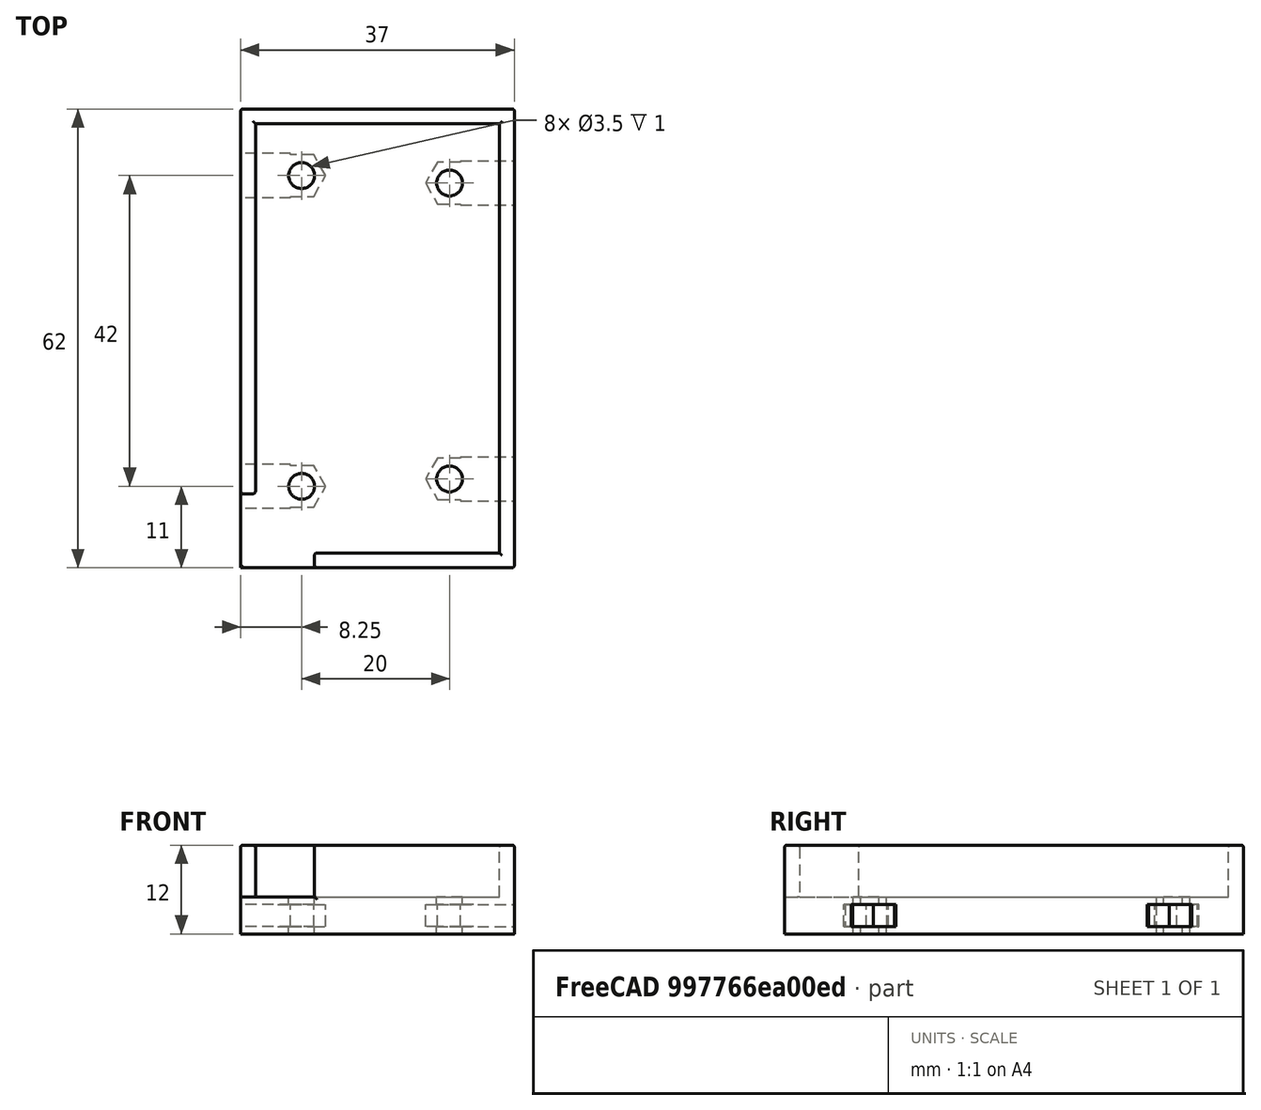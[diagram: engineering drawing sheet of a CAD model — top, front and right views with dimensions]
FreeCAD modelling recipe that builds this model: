
FCSTD DOCUMENT  (FreeCAD 0.19R14555 (Git shallow))
Label: Soporte Bateria
License: All rights reserved
LicenseURL: http://en.wikipedia.org/wiki/All_rights_reserved
objects: Part::Box×7, Part::MultiFuse×5, Part::Cylinder×4, Part::Prism×4, Part::Cut×3, Part::Fillet×2
note: 25 computed .brp shape members not serialized (recipe doc carries the construction recipe); baked Part::Feature solids carry a one-line shape summary decoded from their .brp

FEATURE [Part::Box] Box  label="Cubo"
  AttacherType = Attacher::AttachEngine3D
  Height = 10
  Length = 33
  Placement = pos=(0,0,5) rot=(0,0,1;0rad)
  Width = 58
FEATURE [Part::Box] Box001  label="Cubo001"
  AttacherType = Attacher::AttachEngine3D
  Height = 12
  Length = 37
  Placement = pos=(-2,-2,0) rot=(0,0,1;0rad)
  Width = 62
FEATURE [Part::Cut] Cut
  Base = -> Box001
  Tool = -> Box
FEATURE [Part::Box] Box002  label="Cubo002"
  AttacherType = Attacher::AttachEngine3D
  Height = 10
  Length = 10
  Placement = pos=(-2,-2,5) rot=(0,0,1;0rad)
  Width = 10
FEATURE [Part::Cut] Cut001
  Base = -> Cut
  Tool = -> Box002
FEATURE [Part::Cylinder] Cylinder004  label="Cilindro004"
  Angle = 360
  AttacherType = Attacher::AttachEngine3D
  Height = 20
  Placement = pos=(34,7.5,-1) rot=(0,0,1;0rad)
  Radius = 1.75
FEATURE [Part::Prism] Prism002  label="Prisma002"
  AttacherType = Attacher::AttachEngine3D
  Circumradius = 3.25
  FirstAngle = 0
  Height = 3
  Placement = pos=(34,7.5,3) rot=(0,0,1;1.5708rad)
  Polygon = 6
  SecondAngle = 0
FEATURE [Part::Box] Box003  label="Cubo003"
  AttacherType = Attacher::AttachEngine3D
  Height = 3
  Length = 6
  Placement = pos=(31,9,3) rot=(0,0,1;0rad)
  Width = 20
FEATURE [Part::MultiFuse] Fusion
  Placement = pos=(13.75,17,-2) rot=(0,0,1;1.5708rad)
  Shapes = -> [Box003,Prism002,Cylinder004]
FEATURE [Part::Box] Box004  label="Cubo004"
  AttacherType = Attacher::AttachEngine3D
  Height = 3
  Length = 6
  Placement = pos=(31,9,3) rot=(0,0,1;0rad)
  Width = 20
FEATURE [Part::Cylinder] Cylinder005  label="Cilindro005"
  Angle = 360
  AttacherType = Attacher::AttachEngine3D
  Height = 20
  Placement = pos=(34,7.5,-1) rot=(0,0,1;0rad)
  Radius = 1.75
FEATURE [Part::Prism] Prism003  label="Prisma003"
  AttacherType = Attacher::AttachEngine3D
  Circumradius = 3.25
  FirstAngle = 0
  Height = 3
  Placement = pos=(34,7.5,3) rot=(0,0,1;1.5708rad)
  Polygon = 6
  SecondAngle = 0
FEATURE [Part::MultiFuse] Fusion001
  Placement = pos=(13.75,-25,-2) rot=(0,0,1;1.5708rad)
  Shapes = -> [Box004,Prism003,Cylinder005]
FEATURE [Part::Prism] Prism004  label="Prisma004"
  AttacherType = Attacher::AttachEngine3D
  Circumradius = 3.25
  FirstAngle = 0
  Height = 3
  Placement = pos=(34,7.5,3) rot=(0,0,1;1.5708rad)
  Polygon = 6
  SecondAngle = 0
FEATURE [Part::Cylinder] Cylinder006  label="Cilindro006"
  Angle = 360
  AttacherType = Attacher::AttachEngine3D
  Height = 20
  Placement = pos=(34,7.5,-1) rot=(0,0,1;0rad)
  Radius = 1.75
FEATURE [Part::Box] Box005  label="Cubo005"
  AttacherType = Attacher::AttachEngine3D
  Height = 3
  Length = 6
  Placement = pos=(31,9,3) rot=(0,0,1;0rad)
  Width = 20
FEATURE [Part::MultiFuse] Fusion002
  Placement = pos=(18.75,44,-2) rot=(0,0,1;-1.5708rad)
  Shapes = -> [Box005,Prism004,Cylinder006]
FEATURE [Part::Cylinder] Cylinder007  label="Cilindro007"
  Angle = 360
  AttacherType = Attacher::AttachEngine3D
  Height = 20
  Placement = pos=(34,7.5,-1) rot=(0,0,1;0rad)
  Radius = 1.75
FEATURE [Part::Prism] Prism005  label="Prisma005"
  AttacherType = Attacher::AttachEngine3D
  Circumradius = 3.25
  FirstAngle = 0
  Height = 3
  Placement = pos=(34,7.5,3) rot=(0,0,1;1.5708rad)
  Polygon = 6
  SecondAngle = 0
FEATURE [Part::Box] Box006  label="Cubo006"
  AttacherType = Attacher::AttachEngine3D
  Height = 3
  Length = 6
  Placement = pos=(31,9,3) rot=(0,0,1;0rad)
  Width = 20
FEATURE [Part::MultiFuse] Fusion003
  Placement = pos=(18.75,84,-2) rot=(0,0,-1;1.5708rad)
  Shapes = -> [Box006,Prism005,Cylinder007]
FEATURE [Part::MultiFuse] Fusion004
  Shapes = -> [Fusion,Fusion001,Fusion002,Fusion003]
FEATURE [Part::Cut] Cut002
  Base = -> Cut001
  Tool = -> Fusion004
FEATURE [Part::Fillet] Fillet
  Base = -> Cut002
  Edges = 11 edges r=0.3: [Edge4,Edge6,Edge15,Edge16,Edge30,Edge31,Edge34,Edge36,Edge37,Edge38,Edge39]
FEATURE [Part::Fillet] Fillet001
  Base = -> Fillet
  Edges = 8 edges r=0.3: [Edge5,Edge6,Edge27,Edge30,Edge38,Edge39,Edge110,Edge112]
